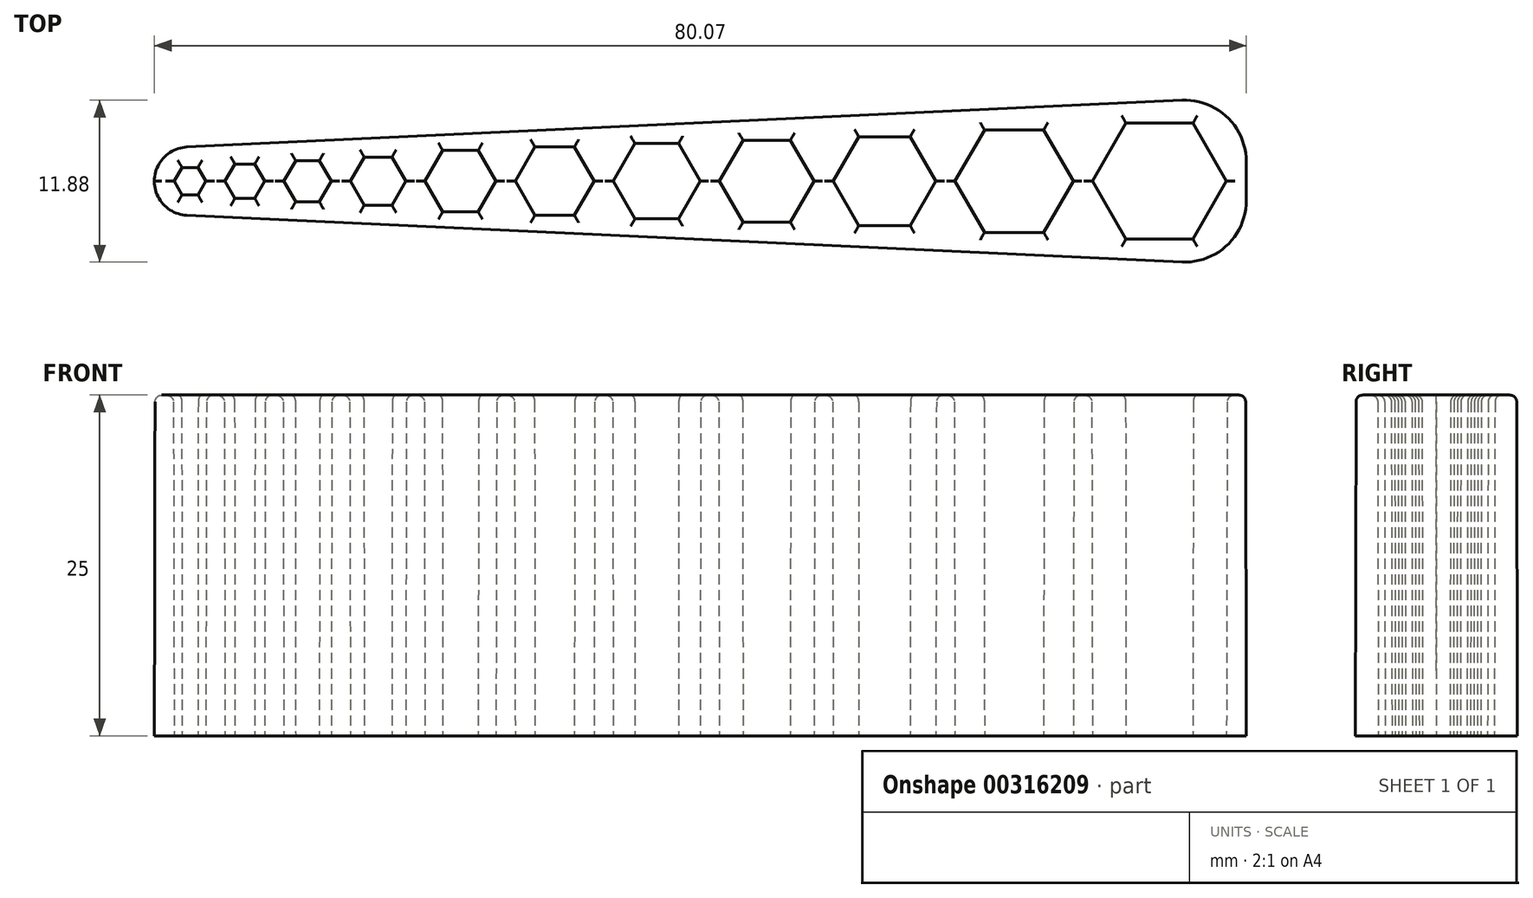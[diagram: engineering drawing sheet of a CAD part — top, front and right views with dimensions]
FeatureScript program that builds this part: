
annotation { "Feature Type Name" : "Feature", "Feature Type Description" : "" }
export const myFeature = defineFeature(function(context is Context, id is Id, definition is map)
    precondition{}
    {
        {
            var Q0;
            Q0=qCreatedBy(makeId("Top.planeOp"),FACE);
            var sketch = newSketch(context, id + "F0", { "sketchPlane" : qUnion([Q0])});
            skCircle(sketch, "E0.cCircle", {"center": v(0, 0) * mm, "radius": 0.75 * mm, "construction": true});
            skLineSegment(sketch, "E0.0", {"start": v(-0.43, 0.75) * mm, "end": v(0.43, 0.75) * mm});
            skLineSegment(sketch, "E0.1", {"start": v(0.43, 0.75) * mm, "end": v(0.87, 0) * mm});
            skLineSegment(sketch, "E0.2", {"start": v(0.87, 0) * mm, "end": v(0.43, -0.75) * mm});
            skLineSegment(sketch, "E0.3", {"start": v(0.43, -0.75) * mm, "end": v(-0.43, -0.75) * mm});
            skLineSegment(sketch, "E0.4", {"start": v(-0.43, -0.75) * mm, "end": v(-0.87, 0) * mm});
            skLineSegment(sketch, "E0.5", {"start": v(-0.87, 0) * mm, "end": v(-0.43, 0.75) * mm});
            skPoint(sketch, "E0.0.midPoint", {"position": v(0, 0.75) * mm});
            skCircle(sketch, "E1.cCircle", {"center": v(4.02, 0) * mm, "radius": 1 * mm, "construction": true});
            skLineSegment(sketch, "E1.0", {"start": v(3.44, 1) * mm, "end": v(4.6, 1) * mm});
            skLineSegment(sketch, "E1.1", {"start": v(4.6, 1) * mm, "end": v(5.18, 0) * mm});
            skLineSegment(sketch, "E1.2", {"start": v(5.18, 0) * mm, "end": v(4.6, -1) * mm});
            skLineSegment(sketch, "E1.3", {"start": v(4.6, -1) * mm, "end": v(3.44, -1) * mm});
            skLineSegment(sketch, "E1.4", {"start": v(3.44, -1) * mm, "end": v(2.87, 0) * mm});
            skLineSegment(sketch, "E1.5", {"start": v(2.87, 0) * mm, "end": v(3.44, 1) * mm});
            skPoint(sketch, "E1.0.midPoint", {"position": v(4.02, 1) * mm});
            skCircle(sketch, "E2.cCircle", {"center": v(8.62, 0) * mm, "radius": 1.25 * mm, "construction": true});
            skLineSegment(sketch, "E2.0", {"start": v(7.9, 1.25) * mm, "end": v(9.34, 1.25) * mm});
            skLineSegment(sketch, "E2.1", {"start": v(9.34, 1.25) * mm, "end": v(10.06, 0) * mm});
            skLineSegment(sketch, "E2.2", {"start": v(10.06, 0) * mm, "end": v(9.34, -1.25) * mm});
            skLineSegment(sketch, "E2.3", {"start": v(9.34, -1.25) * mm, "end": v(7.9, -1.25) * mm});
            skLineSegment(sketch, "E2.4", {"start": v(7.9, -1.25) * mm, "end": v(7.18, 0) * mm});
            skLineSegment(sketch, "E2.5", {"start": v(7.18, 0) * mm, "end": v(7.9, 1.25) * mm});
            skPoint(sketch, "E2.0.midPoint", {"position": v(8.62, 1.25) * mm});
            skCircle(sketch, "E3.cCircle", {"center": v(13.8, 0) * mm, "radius": 1.5 * mm, "construction": true});
            skLineSegment(sketch, "E3.0", {"start": v(12.93, 1.5) * mm, "end": v(14.66, 1.5) * mm});
            skLineSegment(sketch, "E3.1", {"start": v(14.66, 1.5) * mm, "end": v(15.53, 0) * mm});
            skLineSegment(sketch, "E3.2", {"start": v(15.53, 0) * mm, "end": v(14.66, -1.5) * mm});
            skLineSegment(sketch, "E3.3", {"start": v(14.66, -1.5) * mm, "end": v(12.93, -1.5) * mm});
            skLineSegment(sketch, "E3.4", {"start": v(12.93, -1.5) * mm, "end": v(12.06, 0) * mm});
            skLineSegment(sketch, "E3.5", {"start": v(12.06, 0) * mm, "end": v(12.93, 1.5) * mm});
            skPoint(sketch, "E3.0.midPoint", {"position": v(13.8, 1.5) * mm});
            skCircle(sketch, "E4.cCircle", {"center": v(19.84, 0) * mm, "radius": 2 * mm, "construction": true});
            skLineSegment(sketch, "E4.0", {"start": v(18.68, 2) * mm, "end": v(21, 2) * mm});
            skLineSegment(sketch, "E4.1", {"start": v(21, 2) * mm, "end": v(22.15, 0) * mm});
            skLineSegment(sketch, "E4.2", {"start": v(22.15, 0) * mm, "end": v(21, -2) * mm});
            skLineSegment(sketch, "E4.3", {"start": v(21, -2) * mm, "end": v(18.68, -2) * mm});
            skLineSegment(sketch, "E4.4", {"start": v(18.68, -2) * mm, "end": v(17.53, 0) * mm});
            skLineSegment(sketch, "E4.5", {"start": v(17.53, 0) * mm, "end": v(18.68, 2) * mm});
            skPoint(sketch, "E4.0.midPoint", {"position": v(19.84, 2) * mm});
            skCircle(sketch, "E5.cCircle", {"center": v(26.74, 0) * mm, "radius": 2.25 * mm, "construction": true});
            skLineSegment(sketch, "E5.0", {"start": v(25.44, 2.25) * mm, "end": v(28.04, 2.25) * mm});
            skLineSegment(sketch, "E5.1", {"start": v(28.04, 2.25) * mm, "end": v(29.34, 0) * mm});
            skLineSegment(sketch, "E5.2", {"start": v(29.34, 0) * mm, "end": v(28.04, -2.25) * mm});
            skLineSegment(sketch, "E5.3", {"start": v(28.04, -2.25) * mm, "end": v(25.44, -2.25) * mm});
            skLineSegment(sketch, "E5.4", {"start": v(25.44, -2.25) * mm, "end": v(24.15, 0) * mm});
            skLineSegment(sketch, "E5.5", {"start": v(24.15, 0) * mm, "end": v(25.44, 2.25) * mm});
            skPoint(sketch, "E5.0.midPoint", {"position": v(26.74, 2.25) * mm});
            skCircle(sketch, "E6.cCircle", {"center": v(34.23, 0) * mm, "radius": 2.5 * mm, "construction": true});
            skLineSegment(sketch, "E6.0", {"start": v(32.78, 2.5) * mm, "end": v(35.67, 2.5) * mm});
            skLineSegment(sketch, "E6.1", {"start": v(35.67, 2.5) * mm, "end": v(37.11, 0) * mm});
            skLineSegment(sketch, "E6.2", {"start": v(37.11, 0) * mm, "end": v(35.67, -2.5) * mm});
            skLineSegment(sketch, "E6.3", {"start": v(35.67, -2.5) * mm, "end": v(32.78, -2.5) * mm});
            skLineSegment(sketch, "E6.4", {"start": v(32.78, -2.5) * mm, "end": v(31.34, 0) * mm});
            skLineSegment(sketch, "E6.5", {"start": v(31.34, 0) * mm, "end": v(32.78, 2.5) * mm});
            skPoint(sketch, "E6.0.midPoint", {"position": v(34.23, 2.5) * mm});
            skCircle(sketch, "E7.cCircle", {"center": v(42.3, 0) * mm, "radius": 2.75 * mm, "construction": true});
            skLineSegment(sketch, "E7.0", {"start": v(40.7, 2.75) * mm, "end": v(43.88, 2.75) * mm});
            skLineSegment(sketch, "E7.1", {"start": v(43.88, 2.75) * mm, "end": v(45.47, 0) * mm});
            skLineSegment(sketch, "E7.2", {"start": v(45.47, 0) * mm, "end": v(43.88, -2.75) * mm});
            skLineSegment(sketch, "E7.3", {"start": v(43.88, -2.75) * mm, "end": v(40.7, -2.75) * mm});
            skLineSegment(sketch, "E7.4", {"start": v(40.7, -2.75) * mm, "end": v(39.11, 0) * mm});
            skLineSegment(sketch, "E7.5", {"start": v(39.11, 0) * mm, "end": v(40.7, 2.75) * mm});
            skPoint(sketch, "E7.0.midPoint", {"position": v(42.3, 2.75) * mm});
            skCircle(sketch, "E8.cCircle", {"center": v(50.93, 0) * mm, "radius": 3 * mm, "construction": true});
            skLineSegment(sketch, "E8.0", {"start": v(49.2, 3) * mm, "end": v(52.66, 3) * mm});
            skLineSegment(sketch, "E8.1", {"start": v(52.66, 3) * mm, "end": v(54.4, 0) * mm});
            skLineSegment(sketch, "E8.2", {"start": v(54.4, 0) * mm, "end": v(52.66, -3) * mm});
            skLineSegment(sketch, "E8.3", {"start": v(52.66, -3) * mm, "end": v(49.2, -3) * mm});
            skLineSegment(sketch, "E8.4", {"start": v(49.2, -3) * mm, "end": v(47.47, 0) * mm});
            skLineSegment(sketch, "E8.5", {"start": v(47.47, 0) * mm, "end": v(49.2, 3) * mm});
            skPoint(sketch, "E8.0.midPoint", {"position": v(50.93, 3) * mm});
            skLineSegment(sketch, "E9", {"start": v(-2.87, 2.64) * mm, "end": v(-2.87, 0) * mm});
            skLineSegment(sketch, "E10", {"start": v(77.71, 0) * mm, "end": v(77.71, 6.42) * mm});
            skLineSegment(sketch, "E11", {"start": v(77.71, 6.42) * mm, "end": v(-2.87, 2.64) * mm});
            skLineSegment(sketch, "E12.MirrorCS", {"start": v(-2.87, -2.64) * mm, "end": v(-2.87, 0) * mm});
            skLineSegment(sketch, "E13.MirrorCS", {"start": v(77.71, -6.42) * mm, "end": v(-2.87, -2.64) * mm});
            skLineSegment(sketch, "E14.MirrorCS", {"start": v(77.71, 0) * mm, "end": v(77.71, -6.42) * mm});
            skCircle(sketch, "E15.cCircle", {"center": v(60.44, 0) * mm, "radius": 3.5 * mm, "construction": true});
            skLineSegment(sketch, "E15.0", {"start": v(58.41, 3.5) * mm, "end": v(62.46, 3.5) * mm});
            skLineSegment(sketch, "E15.1", {"start": v(62.46, 3.5) * mm, "end": v(64.48, 0) * mm});
            skLineSegment(sketch, "E15.2", {"start": v(64.48, 0) * mm, "end": v(62.46, -3.5) * mm});
            skLineSegment(sketch, "E15.3", {"start": v(62.46, -3.5) * mm, "end": v(58.41, -3.5) * mm});
            skLineSegment(sketch, "E15.4", {"start": v(58.41, -3.5) * mm, "end": v(56.4, 0) * mm});
            skLineSegment(sketch, "E15.5", {"start": v(56.4, 0) * mm, "end": v(58.41, 3.5) * mm});
            skPoint(sketch, "E15.0.midPoint", {"position": v(60.44, 3.5) * mm});
            skCircle(sketch, "E16.cCircle", {"center": v(71.1, 0) * mm, "radius": 4 * mm, "construction": true});
            skLineSegment(sketch, "E16.0", {"start": v(68.79, 4) * mm, "end": v(73.4, 4) * mm});
            skLineSegment(sketch, "E16.1", {"start": v(73.4, 4) * mm, "end": v(75.71, 0) * mm});
            skLineSegment(sketch, "E16.2", {"start": v(75.71, 0) * mm, "end": v(73.4, -4) * mm});
            skLineSegment(sketch, "E16.3", {"start": v(73.4, -4) * mm, "end": v(68.79, -4) * mm});
            skLineSegment(sketch, "E16.4", {"start": v(68.79, -4) * mm, "end": v(66.48, 0) * mm});
            skLineSegment(sketch, "E16.5", {"start": v(66.48, 0) * mm, "end": v(68.79, 4) * mm});
            skPoint(sketch, "E16.0.midPoint", {"position": v(71.1, 4) * mm});
            skSolve(sketch);
        }
        {
            var Q0;
            Q0=makeQuery(id+"F0.imprint","IMPRINT",FACE,{"disambiguationData":[TD([[makeQuery(id+"F0.imprint","IMPRINT",EDGE,{"derivedFrom":sQuery(id+"F0.wireOp",EDGE,"E0.0")}),1.0]])]});
            extrude(context, id + "F1", {"entities" : qUnion([Q0]), "depth" : 25 * mm});
        }
        {
            var Q0;
            Q0=makeQuery(id+"F1.opExtrude","CAP_FACE",FACE,{"disambiguationData":[OSD([sQuery(id+"F0.wireOp",EDGE,"E0.0"),sQuery(id+"F0.wireOp",EDGE,"E0.1"),sQuery(id+"F0.wireOp",EDGE,"E0.2"),sQuery(id+"F0.wireOp",EDGE,"E0.3"),sQuery(id+"F0.wireOp",EDGE,"E0.4"),sQuery(id+"F0.wireOp",EDGE,"E0.5"),sQuery(id+"F0.wireOp",EDGE,"E1.0"),sQuery(id+"F0.wireOp",EDGE,"E1.1"),sQuery(id+"F0.wireOp",EDGE,"E1.2"),sQuery(id+"F0.wireOp",EDGE,"E1.3"),sQuery(id+"F0.wireOp",EDGE,"E1.4"),sQuery(id+"F0.wireOp",EDGE,"E1.5"),sQuery(id+"F0.wireOp",EDGE,"E2.0"),sQuery(id+"F0.wireOp",EDGE,"E2.1"),sQuery(id+"F0.wireOp",EDGE,"E2.2"),sQuery(id+"F0.wireOp",EDGE,"E2.3"),sQuery(id+"F0.wireOp",EDGE,"E2.4"),sQuery(id+"F0.wireOp",EDGE,"E2.5"),sQuery(id+"F0.wireOp",EDGE,"E3.0"),sQuery(id+"F0.wireOp",EDGE,"E3.1"),sQuery(id+"F0.wireOp",EDGE,"E3.2"),sQuery(id+"F0.wireOp",EDGE,"E3.3"),sQuery(id+"F0.wireOp",EDGE,"E3.4"),sQuery(id+"F0.wireOp",EDGE,"E3.5"),sQuery(id+"F0.wireOp",EDGE,"E4.0"),sQuery(id+"F0.wireOp",EDGE,"E4.1"),sQuery(id+"F0.wireOp",EDGE,"E4.2"),sQuery(id+"F0.wireOp",EDGE,"E4.3"),sQuery(id+"F0.wireOp",EDGE,"E4.4"),sQuery(id+"F0.wireOp",EDGE,"E4.5"),sQuery(id+"F0.wireOp",EDGE,"E5.0"),sQuery(id+"F0.wireOp",EDGE,"E5.1"),sQuery(id+"F0.wireOp",EDGE,"E5.2"),sQuery(id+"F0.wireOp",EDGE,"E5.3"),sQuery(id+"F0.wireOp",EDGE,"E5.4"),sQuery(id+"F0.wireOp",EDGE,"E5.5"),sQuery(id+"F0.wireOp",EDGE,"E6.0"),sQuery(id+"F0.wireOp",EDGE,"E6.1"),sQuery(id+"F0.wireOp",EDGE,"E6.2"),sQuery(id+"F0.wireOp",EDGE,"E6.3"),sQuery(id+"F0.wireOp",EDGE,"E6.4"),sQuery(id+"F0.wireOp",EDGE,"E6.5"),sQuery(id+"F0.wireOp",EDGE,"E7.0"),sQuery(id+"F0.wireOp",EDGE,"E7.1"),sQuery(id+"F0.wireOp",EDGE,"E7.2"),sQuery(id+"F0.wireOp",EDGE,"E7.3"),sQuery(id+"F0.wireOp",EDGE,"E7.4"),sQuery(id+"F0.wireOp",EDGE,"E7.5"),sQuery(id+"F0.wireOp",EDGE,"E8.0"),sQuery(id+"F0.wireOp",EDGE,"E8.1"),sQuery(id+"F0.wireOp",EDGE,"E8.2"),sQuery(id+"F0.wireOp",EDGE,"E8.3"),sQuery(id+"F0.wireOp",EDGE,"E8.4"),sQuery(id+"F0.wireOp",EDGE,"E8.5"),sQuery(id+"F0.wireOp",EDGE,"E9"),sQuery(id+"F0.wireOp",EDGE,"E10"),sQuery(id+"F0.wireOp",EDGE,"E11"),sQuery(id+"F0.wireOp",EDGE,"E12.MirrorCS"),sQuery(id+"F0.wireOp",EDGE,"E13.MirrorCS"),sQuery(id+"F0.wireOp",EDGE,"E14.MirrorCS")])],"isStart":false});
            chamfer(context, id + "F2", {"entities" : qUnion([Q0]), "chamferType" : ChamferType.OFFSET_ANGLE, "width" : 0.3 * mm, "oppositeDirection" : false, "angle" : 89.9 * degree, "tangentPropagation" : true});
        }
        {
            var Q0;
            Q0=makeQuery(id+"F2.opChamfer","BLEND_EDGE",EDGE,{"blendedFrom":[makeQuery(id+"F1.opExtrude","CAP_EDGE",EDGE,{"disambiguationData":[OSD([sQuery(id+"F0.wireOp",EDGE,"E9"),sQuery(id+"F0.wireOp",EDGE,"E12.MirrorCS")])],"isStart":false}),makeQuery(id+"F1.opExtrude","CAP_EDGE",EDGE,{"disambiguationData":[OSD([sQuery(id+"F0.wireOp",EDGE,"E13.MirrorCS")])],"isStart":false})],"blendedInto":[]});
            var Q1;
            Q1=makeQuery(id+"F2.opChamfer","BLEND_EDGE",EDGE,{"blendedFrom":[makeQuery(id+"F1.opExtrude","CAP_EDGE",EDGE,{"disambiguationData":[OSD([sQuery(id+"F0.wireOp",EDGE,"E9"),sQuery(id+"F0.wireOp",EDGE,"E12.MirrorCS")])],"isStart":false}),makeQuery(id+"F1.opExtrude","CAP_EDGE",EDGE,{"disambiguationData":[OSD([sQuery(id+"F0.wireOp",EDGE,"E11")])],"isStart":false})],"blendedInto":[]});
            fillet(context, id + "F3", {"entities" : qUnion([Q0, Q1]), "radius" : 2.5 * mm, "tangentPropagation" : true, "allowEdgeOverflow" : false});
        }
        {
            var Q0;
            Q0=makeQuery(id+"F2.opChamfer","BLEND_EDGE",EDGE,{"blendedFrom":[makeQuery(id+"F1.opExtrude","CAP_EDGE",EDGE,{"disambiguationData":[OSD([sQuery(id+"F0.wireOp",EDGE,"E10"),sQuery(id+"F0.wireOp",EDGE,"E14.MirrorCS")])],"isStart":false}),makeQuery(id+"F1.opExtrude","CAP_EDGE",EDGE,{"disambiguationData":[OSD([sQuery(id+"F0.wireOp",EDGE,"E13.MirrorCS")])],"isStart":false})],"blendedInto":[]});
            var Q1;
            Q1=makeQuery(id+"F2.opChamfer","BLEND_EDGE",EDGE,{"blendedFrom":[makeQuery(id+"F1.opExtrude","CAP_EDGE",EDGE,{"disambiguationData":[OSD([sQuery(id+"F0.wireOp",EDGE,"E10"),sQuery(id+"F0.wireOp",EDGE,"E14.MirrorCS")])],"isStart":false}),makeQuery(id+"F1.opExtrude","CAP_EDGE",EDGE,{"disambiguationData":[OSD([sQuery(id+"F0.wireOp",EDGE,"E11")])],"isStart":false})],"blendedInto":[]});
            fillet(context, id + "F4", {"entities" : qUnion([Q0, Q1]), "radius" : 4.5 * mm, "tangentPropagation" : true, "allowEdgeOverflow" : false});
        }
        {
            var Q0;
            Q0=makeQuery(id+"F1.opExtrude","CAP_FACE",FACE,{"disambiguationData":[OSD([sQuery(id+"F0.wireOp",EDGE,"E0.0"),sQuery(id+"F0.wireOp",EDGE,"E0.1"),sQuery(id+"F0.wireOp",EDGE,"E0.2"),sQuery(id+"F0.wireOp",EDGE,"E0.3"),sQuery(id+"F0.wireOp",EDGE,"E0.4"),sQuery(id+"F0.wireOp",EDGE,"E0.5"),sQuery(id+"F0.wireOp",EDGE,"E1.0"),sQuery(id+"F0.wireOp",EDGE,"E1.1"),sQuery(id+"F0.wireOp",EDGE,"E1.2"),sQuery(id+"F0.wireOp",EDGE,"E1.3"),sQuery(id+"F0.wireOp",EDGE,"E1.4"),sQuery(id+"F0.wireOp",EDGE,"E1.5"),sQuery(id+"F0.wireOp",EDGE,"E2.0"),sQuery(id+"F0.wireOp",EDGE,"E2.1"),sQuery(id+"F0.wireOp",EDGE,"E2.2"),sQuery(id+"F0.wireOp",EDGE,"E2.3"),sQuery(id+"F0.wireOp",EDGE,"E2.4"),sQuery(id+"F0.wireOp",EDGE,"E2.5"),sQuery(id+"F0.wireOp",EDGE,"E3.0"),sQuery(id+"F0.wireOp",EDGE,"E3.1"),sQuery(id+"F0.wireOp",EDGE,"E3.2"),sQuery(id+"F0.wireOp",EDGE,"E3.3"),sQuery(id+"F0.wireOp",EDGE,"E3.4"),sQuery(id+"F0.wireOp",EDGE,"E3.5"),sQuery(id+"F0.wireOp",EDGE,"E4.0"),sQuery(id+"F0.wireOp",EDGE,"E4.1"),sQuery(id+"F0.wireOp",EDGE,"E4.2"),sQuery(id+"F0.wireOp",EDGE,"E4.3"),sQuery(id+"F0.wireOp",EDGE,"E4.4"),sQuery(id+"F0.wireOp",EDGE,"E4.5"),sQuery(id+"F0.wireOp",EDGE,"E5.0"),sQuery(id+"F0.wireOp",EDGE,"E5.1"),sQuery(id+"F0.wireOp",EDGE,"E5.2"),sQuery(id+"F0.wireOp",EDGE,"E5.3"),sQuery(id+"F0.wireOp",EDGE,"E5.4"),sQuery(id+"F0.wireOp",EDGE,"E5.5"),sQuery(id+"F0.wireOp",EDGE,"E6.0"),sQuery(id+"F0.wireOp",EDGE,"E6.1"),sQuery(id+"F0.wireOp",EDGE,"E6.2"),sQuery(id+"F0.wireOp",EDGE,"E6.3"),sQuery(id+"F0.wireOp",EDGE,"E6.4"),sQuery(id+"F0.wireOp",EDGE,"E6.5"),sQuery(id+"F0.wireOp",EDGE,"E7.0"),sQuery(id+"F0.wireOp",EDGE,"E7.1"),sQuery(id+"F0.wireOp",EDGE,"E7.2"),sQuery(id+"F0.wireOp",EDGE,"E7.3"),sQuery(id+"F0.wireOp",EDGE,"E7.4"),sQuery(id+"F0.wireOp",EDGE,"E7.5"),sQuery(id+"F0.wireOp",EDGE,"E8.0"),sQuery(id+"F0.wireOp",EDGE,"E8.1"),sQuery(id+"F0.wireOp",EDGE,"E8.2"),sQuery(id+"F0.wireOp",EDGE,"E8.3"),sQuery(id+"F0.wireOp",EDGE,"E8.4"),sQuery(id+"F0.wireOp",EDGE,"E8.5"),sQuery(id+"F0.wireOp",EDGE,"E9"),sQuery(id+"F0.wireOp",EDGE,"E10"),sQuery(id+"F0.wireOp",EDGE,"E11"),sQuery(id+"F0.wireOp",EDGE,"E12.MirrorCS"),sQuery(id+"F0.wireOp",EDGE,"E13.MirrorCS"),sQuery(id+"F0.wireOp",EDGE,"E14.MirrorCS")])],"isStart":false});
            fillet(context, id + "F5", {"entities" : qUnion([Q0]), "radius" : 0.5 * mm, "tangentPropagation" : true, "allowEdgeOverflow" : false});
        }
    });
